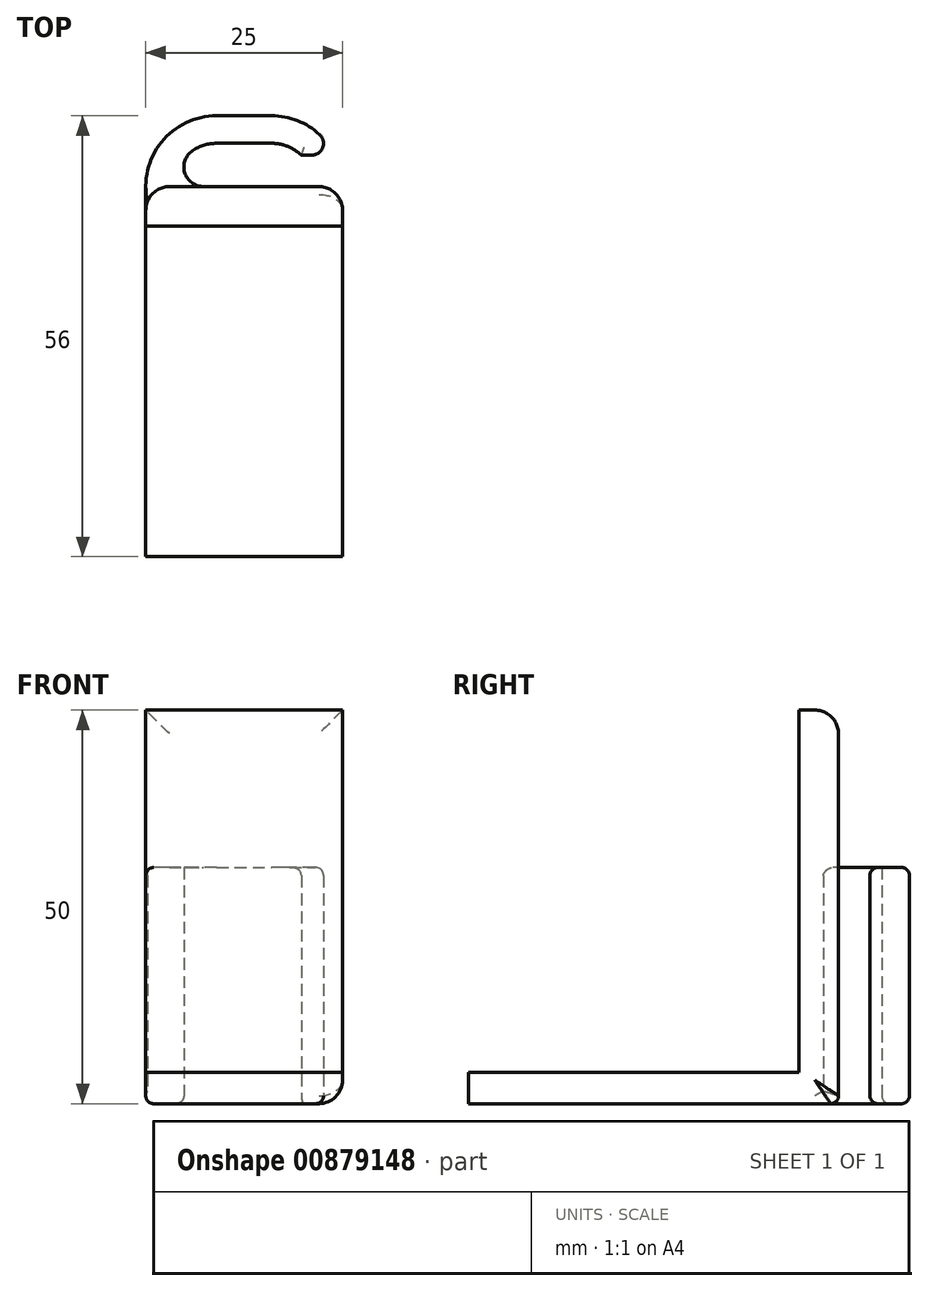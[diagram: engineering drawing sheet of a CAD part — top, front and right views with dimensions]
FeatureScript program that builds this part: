
annotation { "Feature Type Name" : "Feature", "Feature Type Description" : "" }
export const myFeature = defineFeature(function(context is Context, id is Id, definition is map)
    precondition{}
    {
        {
            var Q0;
            Q0=qCreatedBy(makeId("Top.planeOp"),FACE);
            var sketch = newSketch(context, id + "F0", { "sketchPlane" : qUnion([Q0])});
            skLineSegment(sketch, "E0.bottom", {"start": v(0, 0) * mm, "end": v(25, 0) * mm});
            skLineSegment(sketch, "E0.top", {"start": v(0, 47) * mm, "end": v(25, 47) * mm});
            skLineSegment(sketch, "E0.left", {"start": v(0, 0) * mm, "end": v(0, 47) * mm});
            skLineSegment(sketch, "E0.right", {"start": v(25, 0) * mm, "end": v(25, 47) * mm});
            skLineSegment(sketch, "E1.bottom", {"start": v(25, 0) * mm, "end": v(0, 0) * mm});
            skLineSegment(sketch, "E1.top", {"start": v(25, 5) * mm, "end": v(0, 5) * mm});
            skLineSegment(sketch, "E1.left", {"start": v(25, 0) * mm, "end": v(25, 5) * mm});
            skLineSegment(sketch, "E1.right", {"start": v(0, 0) * mm, "end": v(0, 5) * mm});
            skLineSegment(sketch, "E2.top", {"start": v(0, 42) * mm, "end": v(25, 42) * mm});
            skLineSegment(sketch, "E2.left", {"start": v(0, 47) * mm, "end": v(0, 42) * mm});
            skLineSegment(sketch, "E2.right", {"start": v(25, 47) * mm, "end": v(25, 42) * mm});
            skLineSegment(sketch, "E3.bottom", {"start": v(7.34, 47) * mm, "end": v(24.99, 47) * mm});
            skLineSegment(sketch, "E3.top", {"start": v(9, 56) * mm, "end": v(15.99, 56) * mm});
            skLineSegment(sketch, "E3.left", {"start": v(0, 47) * mm, "end": v(0, 47) * mm});
            skLineSegment(sketch, "E3.right", {"start": v(24.99, 47) * mm, "end": v(24.99, 47) * mm});
            skPoint(sketch, "E4.visualSharp", {"position": v(0, 56) * mm});
            skArc(sketch, "E4.filletArc", {"start": v(9, 56) * mm, "mid": v(2.64, 53.36) * mm, "end": v(0, 47) * mm});
            skPoint(sketch, "E5.visualSharp", {"position": v(24.99, 56) * mm});
            skArc(sketch, "E5.filletArc", {"start": v(22.1, 53.6) * mm, "mid": v(19.27, 55.38) * mm, "end": v(15.99, 56) * mm});
            skArc(sketch, "E6.0", {"start": v(9, 52.5) * mm, "mid": v(7.41, 52.27) * mm, "end": v(5.96, 51.58) * mm});
            skLineSegment(sketch, "E6.1", {"start": v(9, 52.5) * mm, "end": v(15.99, 52.5) * mm});
            skArc(sketch, "E6.2", {"start": v(19.76, 51) * mm, "mid": v(18.02, 52.11) * mm, "end": v(15.99, 52.5) * mm});
            skLineSegment(sketch, "E7", {"start": v(19.76, 51) * mm, "end": v(21.08, 51) * mm});
            skPoint(sketch, "E8.visualSharp", {"position": v(24.05, 51) * mm});
            skArc(sketch, "E8.filletArc", {"start": v(21.08, 51) * mm, "mid": v(22.48, 51.95) * mm, "end": v(22.1, 53.6) * mm});
            skArc(sketch, "E9.filletArc", {"start": v(5.96, 51.58) * mm, "mid": v(4.95, 48.78) * mm, "end": v(7.34, 47) * mm});
            skSolve(sketch);
        }
        {
            var Q0;
            Q0=makeQuery(id+"F0.imprint","IMPRINT",FACE,{"disambiguationData":[TD([[makeQuery(id+"F0.imprint","IMPRINT",EDGE,{"derivedFrom":sQuery(id+"F0.wireOp",EDGE,"E0.left")}),-1.0]])]});
            extrude(context, id + "F1", {"entities" : qUnion([Q0]), "depth" : 4 * mm, "offsetDistance" : 25 * mm});
        }
        {
            var Q0;
            Q0=makeQuery(id+"F0.imprint","IMPRINT",FACE,{"disambiguationData":[TD([[makeQuery(id+"F0.imprint","IMPRINT",EDGE,{"derivedFrom":sQuery(id+"F0.wireOp",EDGE,"E2.top")}),1.0]])]});
            var Q1;
            Q1=makeQuery(id+"F0.imprint","IMPRINT",FACE,{"disambiguationData":[TD([[makeQuery(id+"F0.imprint","IMPRINT",EDGE,{"derivedFrom":sQuery(id+"F0.wireOp",EDGE,"E1.bottom")}),-1.0]])]});
            extrude(context, id + "F2", {"entities" : qUnion([Q0, Q1]), "operationType" : NewBodyOperationType.ADD, "depth" : 50 * mm, "offsetDistance" : 25 * mm});
        }
        {
            var Q0;
            Q0=makeQuery(id+"F0.imprint","IMPRINT",FACE,{"disambiguationData":[TD([[makeQuery(id+"F0.imprint","IMPRINT",EDGE,{"derivedFrom":sQuery(id+"F0.wireOp",EDGE,"E3.top")}),-1.0]])]});
            extrude(context, id + "F3", {"entities" : qUnion([Q0]), "operationType" : NewBodyOperationType.ADD, "depth" : 30 * mm, "offsetDistance" : 25 * mm});
        }
        {
            var Q0;
            Q0=makeQuery(id+"F2.boolean.opBoolean","MERGE",EDGE,{"derivedFrom":[makeQuery(id+"F1.opExtrude","CAP_EDGE",EDGE,{"disambiguationData":[OSD([sQuery(id+"F0.wireOp",EDGE,"E0.left")])],"isStart":true}),makeQuery(id+"F2.opExtrude","CAP_EDGE",EDGE,{"disambiguationData":[OSD([sQuery(id+"F0.wireOp",EDGE,"E1.right")])],"isStart":true}),makeQuery(id+"F2.opExtrude","CAP_EDGE",EDGE,{"disambiguationData":[OSD([sQuery(id+"F0.wireOp",EDGE,"E2.left")])],"isStart":true})]});
            var Q1;
            Q1=makeQuery(id+"F3.opExtrude","CAP_EDGE",EDGE,{"disambiguationData":[OSD([sQuery(id+"F0.wireOp",EDGE,"E4.filletArc")])],"isStart":false});
            var Q2;
            Q2=makeQuery(id+"F2.opExtrude","CAP_EDGE",EDGE,{"disambiguationData":[OSD([sQuery(id+"F0.wireOp",EDGE,"E0.top"),sQuery(id+"F0.wireOp",EDGE,"E3.bottom")])],"isStart":true});
            fillet(context, id + "F4", {"entities" : qUnion([Q0, Q1, Q2]), "radius" : 1 * mm, "tangentPropagation" : true, "allowEdgeOverflow" : false});
        }
        {
            var Q0;
            Q0=makeQuery(id+"F2.opExtrude","SWEPT_FACE",FACE,{"disambiguationData":[OSD([sQuery(id+"F0.wireOp",EDGE,"E1.bottom")])]});
            var Q1;
            Q1=makeQuery(id+"F2.boolean.opBoolean","MERGE",EDGE,{"derivedFrom":[makeQuery(id+"F1.opExtrude","CAP_EDGE",EDGE,{"disambiguationData":[OSD([sQuery(id+"F0.wireOp",EDGE,"E0.right")])],"isStart":true}),makeQuery(id+"F2.opExtrude","CAP_EDGE",EDGE,{"disambiguationData":[OSD([sQuery(id+"F0.wireOp",EDGE,"E1.left")])],"isStart":true}),makeQuery(id+"F2.opExtrude","CAP_EDGE",EDGE,{"disambiguationData":[OSD([sQuery(id+"F0.wireOp",EDGE,"E2.right")])],"isStart":true})]});
            var Q2;
            Q2=makeQuery(id+"F2.opExtrude","SWEPT_EDGE",EDGE,{"disambiguationData":[OSD([sQuery(id+"F0.wireOp",EDGE,"E0.top"),sQuery(id+"F0.wireOp",EDGE,"E2.right")])]});
            var Q3;
            Q3=makeQuery(id+"F2.opExtrude","CAP_EDGE",EDGE,{"disambiguationData":[OSD([sQuery(id+"F0.wireOp",EDGE,"E0.top"),sQuery(id+"F0.wireOp",EDGE,"E3.bottom")])],"isStart":false});
            var Q4;
            Q4=makeQuery(id+"F3.boolean.opBoolean","SPLIT",EDGE,{"derivedFrom":makeQuery(id+"F2.opExtrude","SWEPT_EDGE",EDGE,{"disambiguationData":[OSD([sQuery(id+"F0.wireOp",EDGE,"E0.top"),sQuery(id+"F0.wireOp",EDGE,"E2.left"),sQuery(id+"F0.wireOp",EDGE,"E4.filletArc")])]})});
            var Q5;
            Q5=makeQuery(id+"F2.opExtrude","CAP_EDGE",EDGE,{"disambiguationData":[OSD([sQuery(id+"F0.wireOp",EDGE,"E2.left")])],"isStart":false});
            var Q6;
            Q6=makeQuery(id+"F2.opExtrude","CAP_EDGE",EDGE,{"disambiguationData":[OSD([sQuery(id+"F0.wireOp",EDGE,"E2.right")])],"isStart":false});
            var Q7;
            Q7=makeQuery(id+"F2.opExtrude","CAP_EDGE",EDGE,{"disambiguationData":[OSD([sQuery(id+"F0.wireOp",EDGE,"E0.top"),sQuery(id+"F0.wireOp",EDGE,"E3.bottom")])],"isStart":true});
            var Q8;
            Q8=makeQuery(id+"F2.opExtrude","CAP_EDGE",EDGE,{"disambiguationData":[OSD([sQuery(id+"F0.wireOp",EDGE,"E1.left")])],"isStart":false});
            var Q9;
            Q9=makeQuery(id+"F2.opExtrude","CAP_EDGE",EDGE,{"disambiguationData":[OSD([sQuery(id+"F0.wireOp",EDGE,"E1.right")])],"isStart":false});
            fillet(context, id + "F5", {"entities" : qUnion([Q0, Q1, Q2, Q3, Q4, Q5, Q6, Q7, Q8, Q9]), "radius" : 3 * mm, "tangentPropagation" : true, "allowEdgeOverflow" : false});
        }
    });
